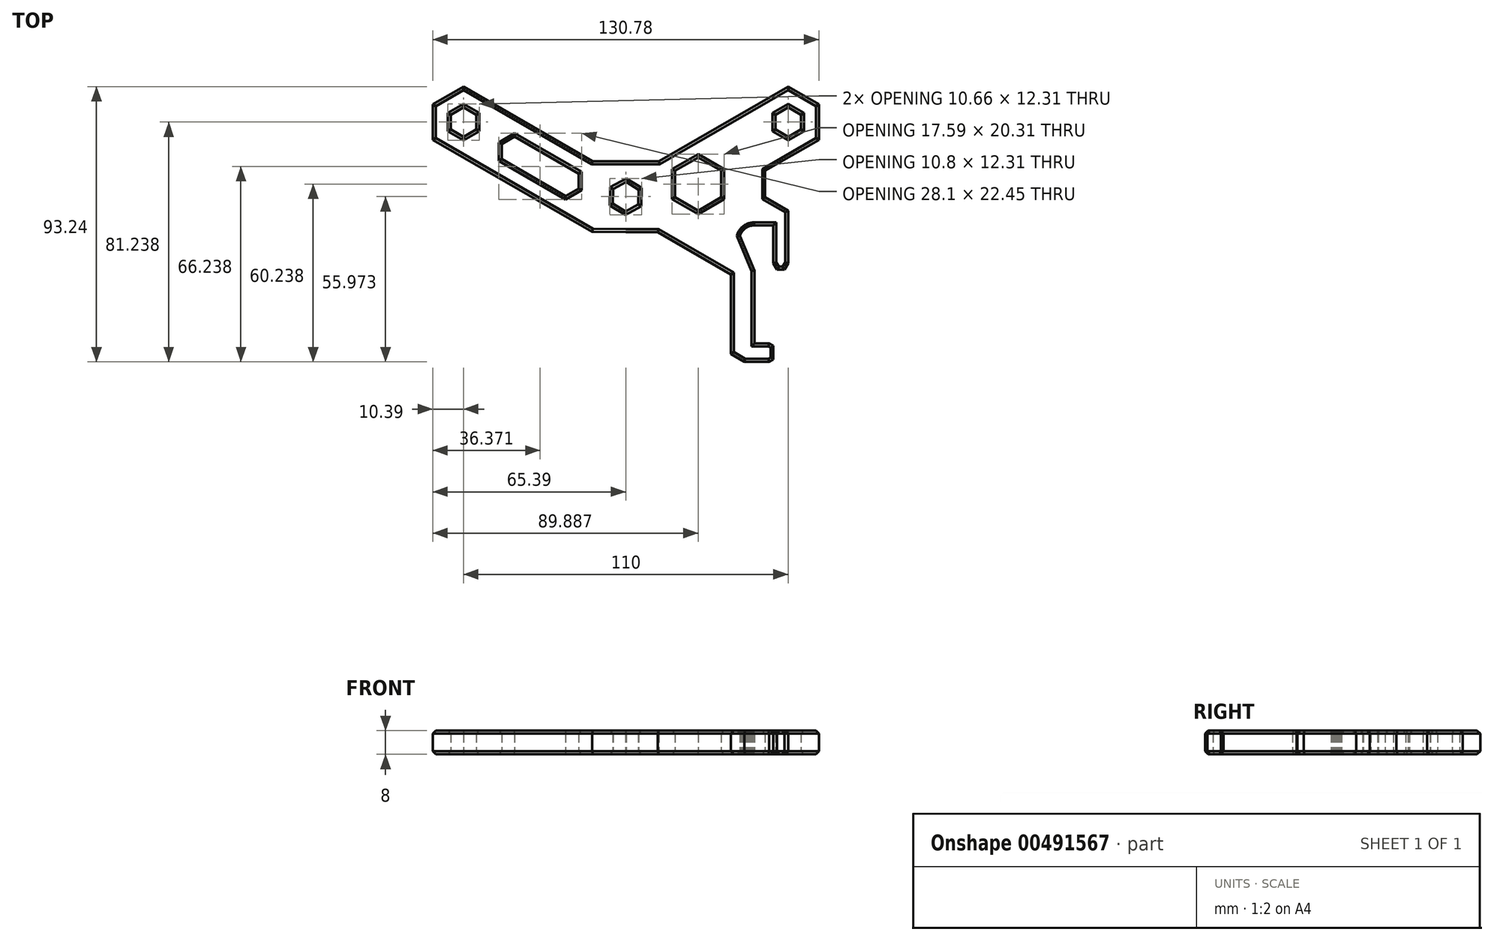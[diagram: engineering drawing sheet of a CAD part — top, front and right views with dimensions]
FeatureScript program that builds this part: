
annotation { "Feature Type Name" : "Feature", "Feature Type Description" : "" }
export const myFeature = defineFeature(function(context is Context, id is Id, definition is map)
    precondition{}
    {
        {
            var Q0;
            Q0=qCreatedBy(makeId("Top.planeOp"),FACE);
            var sketch = newSketch(context, id + "F0", { "sketchPlane" : qUnion([Q0])});
            skLineSegment(sketch, "E0", {"start": v(-65.4, 28.62) * mm, "end": v(-11.37, -2.57) * mm});
            skLineSegment(sketch, "E1", {"start": v(-11.37, -2.57) * mm, "end": v(0, -2.65) * mm});
            skLineSegment(sketch, "E2", {"start": v(0, -2.65) * mm, "end": v(10.81, -2.65) * mm});
            skLineSegment(sketch, "E3", {"start": v(10.81, -2.65) * mm, "end": v(35.6, -16.96) * mm});
            skLineSegment(sketch, "E4", {"start": v(35.6, -16.96) * mm, "end": v(35.6, -43.93) * mm});
            skLineSegment(sketch, "E5", {"start": v(35.6, -43.93) * mm, "end": v(40.17, -46.62) * mm});
            skLineSegment(sketch, "E6", {"start": v(40.17, -46.62) * mm, "end": v(48.6, -46.62) * mm});
            skLineSegment(sketch, "E7", {"start": v(48.6, -46.62) * mm, "end": v(50, -45.83) * mm});
            skLineSegment(sketch, "E8", {"start": v(50, -45.83) * mm, "end": v(50, -41.2) * mm});
            skLineSegment(sketch, "E9", {"start": v(50, -41.2) * mm, "end": v(48.6, -40.38) * mm});
            skLineSegment(sketch, "E10", {"start": v(48.6, -40.38) * mm, "end": v(43.6, -40.38) * mm});
            skLineSegment(sketch, "E11", {"start": v(43.6, -40.38) * mm, "end": v(43.6, -15.68) * mm});
            skLineSegment(sketch, "E12", {"start": v(43.6, -15.68) * mm, "end": v(38.65, -3.92) * mm});
            skLineSegment(sketch, "E13", {"start": v(38.65, -3.92) * mm, "end": v(38.7, -3.76) * mm});
            skLineSegment(sketch, "E14", {"start": v(38.7, -3.76) * mm, "end": v(38.77, -3.6) * mm});
            skLineSegment(sketch, "E15", {"start": v(38.77, -3.6) * mm, "end": v(38.83, -3.43) * mm});
            skLineSegment(sketch, "E16", {"start": v(38.83, -3.43) * mm, "end": v(38.9, -3.28) * mm});
            skLineSegment(sketch, "E17", {"start": v(38.9, -3.28) * mm, "end": v(38.98, -3.12) * mm});
            skLineSegment(sketch, "E18", {"start": v(38.98, -3.12) * mm, "end": v(39.06, -2.97) * mm});
            skLineSegment(sketch, "E19", {"start": v(39.06, -2.97) * mm, "end": v(39.15, -2.82) * mm});
            skLineSegment(sketch, "E20", {"start": v(39.15, -2.82) * mm, "end": v(39.24, -2.67) * mm});
            skLineSegment(sketch, "E21", {"start": v(39.24, -2.67) * mm, "end": v(39.34, -2.53) * mm});
            skLineSegment(sketch, "E22", {"start": v(39.34, -2.53) * mm, "end": v(39.44, -2.39) * mm});
            skLineSegment(sketch, "E23", {"start": v(39.44, -2.39) * mm, "end": v(39.55, -2.25) * mm});
            skLineSegment(sketch, "E24", {"start": v(39.55, -2.25) * mm, "end": v(39.66, -2.12) * mm});
            skLineSegment(sketch, "E25", {"start": v(39.66, -2.12) * mm, "end": v(39.77, -1.99) * mm});
            skLineSegment(sketch, "E26", {"start": v(39.77, -1.99) * mm, "end": v(39.9, -1.86) * mm});
            skLineSegment(sketch, "E27", {"start": v(39.9, -1.86) * mm, "end": v(40.02, -1.74) * mm});
            skLineSegment(sketch, "E28", {"start": v(40.02, -1.74) * mm, "end": v(40.15, -1.63) * mm});
            skLineSegment(sketch, "E29", {"start": v(40.15, -1.63) * mm, "end": v(40.28, -1.52) * mm});
            skLineSegment(sketch, "E30", {"start": v(40.28, -1.52) * mm, "end": v(40.42, -1.4) * mm});
            skLineSegment(sketch, "E31", {"start": v(40.42, -1.4) * mm, "end": v(40.56, -1.3) * mm});
            skLineSegment(sketch, "E32", {"start": v(40.56, -1.3) * mm, "end": v(40.7, -1.2) * mm});
            skLineSegment(sketch, "E33", {"start": v(40.7, -1.2) * mm, "end": v(40.85, -1.12) * mm});
            skLineSegment(sketch, "E34", {"start": v(40.85, -1.12) * mm, "end": v(41, -1.03) * mm});
            skLineSegment(sketch, "E35", {"start": v(41, -1.03) * mm, "end": v(41.15, -0.95) * mm});
            skLineSegment(sketch, "E36", {"start": v(41.15, -0.95) * mm, "end": v(41.3, -0.87) * mm});
            skLineSegment(sketch, "E37", {"start": v(41.3, -0.87) * mm, "end": v(41.46, -0.8) * mm});
            skLineSegment(sketch, "E38", {"start": v(41.46, -0.8) * mm, "end": v(41.62, -0.73) * mm});
            skLineSegment(sketch, "E39", {"start": v(41.62, -0.73) * mm, "end": v(41.78, -0.67) * mm});
            skLineSegment(sketch, "E40", {"start": v(41.78, -0.67) * mm, "end": v(41.95, -0.62) * mm});
            skLineSegment(sketch, "E41", {"start": v(41.95, -0.62) * mm, "end": v(42.12, -0.57) * mm});
            skLineSegment(sketch, "E42", {"start": v(42.12, -0.57) * mm, "end": v(42.28, -0.52) * mm});
            skLineSegment(sketch, "E43", {"start": v(42.28, -0.52) * mm, "end": v(42.45, -0.49) * mm});
            skLineSegment(sketch, "E44", {"start": v(42.45, -0.49) * mm, "end": v(42.62, -0.45) * mm});
            skLineSegment(sketch, "E45", {"start": v(42.62, -0.45) * mm, "end": v(42.8, -0.43) * mm});
            skLineSegment(sketch, "E46", {"start": v(42.8, -0.43) * mm, "end": v(42.97, -0.4) * mm});
            skLineSegment(sketch, "E47", {"start": v(42.97, -0.4) * mm, "end": v(43.14, -0.4) * mm});
            skLineSegment(sketch, "E48", {"start": v(43.14, -0.4) * mm, "end": v(43.31, -0.39) * mm});
            skLineSegment(sketch, "E49", {"start": v(43.31, -0.39) * mm, "end": v(43.49, -0.38) * mm});
            skLineSegment(sketch, "E50", {"start": v(43.49, -0.38) * mm, "end": v(50, -0.38) * mm});
            skLineSegment(sketch, "E51", {"start": v(50, -0.38) * mm, "end": v(50, -13.16) * mm});
            skLineSegment(sketch, "E52", {"start": v(50, -13.16) * mm, "end": v(51.25, -15.33) * mm});
            skLineSegment(sketch, "E53", {"start": v(51.25, -15.33) * mm, "end": v(53.75, -15.33) * mm});
            skLineSegment(sketch, "E54", {"start": v(53.75, -15.33) * mm, "end": v(55, -13.16) * mm});
            skLineSegment(sketch, "E55", {"start": v(55, -13.16) * mm, "end": v(55, 4.62) * mm});
            skLineSegment(sketch, "E56", {"start": v(55, 4.62) * mm, "end": v(47.2, 9.12) * mm});
            skLineSegment(sketch, "E57", {"start": v(47.2, 9.12) * mm, "end": v(47.2, 18.12) * mm});
            skLineSegment(sketch, "E58", {"start": v(47.2, 18.12) * mm, "end": v(55, 22.62) * mm});
            skLineSegment(sketch, "E59", {"start": v(55, 22.62) * mm, "end": v(65.4, 28.62) * mm});
            skLineSegment(sketch, "E60", {"start": v(65.4, 28.62) * mm, "end": v(65.4, 40.62) * mm});
            skLineSegment(sketch, "E61", {"start": v(65.4, 40.62) * mm, "end": v(55, 46.62) * mm});
            skLineSegment(sketch, "E62", {"start": v(55, 46.62) * mm, "end": v(11.24, 21.35) * mm});
            skLineSegment(sketch, "E63", {"start": v(11.24, 21.35) * mm, "end": v(-11.24, 21.35) * mm});
            skLineSegment(sketch, "E64", {"start": v(-11.24, 21.35) * mm, "end": v(-55, 46.62) * mm});
            skLineSegment(sketch, "E65", {"start": v(-55, 46.62) * mm, "end": v(-65.4, 40.62) * mm});
            skLineSegment(sketch, "E66", {"start": v(-65.4, 40.62) * mm, "end": v(-65.4, 28.62) * mm});
            skLineSegment(sketch, "E67", {"start": v(-59.33, 32.12) * mm, "end": v(-59.33, 37.12) * mm});
            skLineSegment(sketch, "E68", {"start": v(-59.33, 37.12) * mm, "end": v(-55, 39.62) * mm});
            skLineSegment(sketch, "E69", {"start": v(-55, 39.62) * mm, "end": v(-50.67, 37.12) * mm});
            skLineSegment(sketch, "E70", {"start": v(-50.67, 37.12) * mm, "end": v(-50.67, 32.12) * mm});
            skLineSegment(sketch, "E71", {"start": v(-50.67, 32.12) * mm, "end": v(-55, 29.62) * mm});
            skLineSegment(sketch, "E72", {"start": v(-55, 29.62) * mm, "end": v(-59.33, 32.12) * mm});
            skLineSegment(sketch, "E73", {"start": v(-42.07, 22.08) * mm, "end": v(-42.07, 27.15) * mm});
            skLineSegment(sketch, "E74", {"start": v(-42.07, 27.15) * mm, "end": v(-37.68, 29.69) * mm});
            skLineSegment(sketch, "E75", {"start": v(-37.68, 29.69) * mm, "end": v(-15.97, 17.15) * mm});
            skLineSegment(sketch, "E76", {"start": v(-15.97, 17.15) * mm, "end": v(-15.97, 12.08) * mm});
            skLineSegment(sketch, "E77", {"start": v(-15.97, 12.08) * mm, "end": v(-20.36, 9.55) * mm});
            skLineSegment(sketch, "E78", {"start": v(-20.36, 9.55) * mm, "end": v(-42.07, 22.08) * mm});
            skLineSegment(sketch, "E79", {"start": v(-4.39, 6.96) * mm, "end": v(-4.27, 11.95) * mm});
            skLineSegment(sketch, "E80", {"start": v(-4.27, 11.95) * mm, "end": v(0.12, 14.35) * mm});
            skLineSegment(sketch, "E81", {"start": v(0.12, 14.35) * mm, "end": v(4.39, 11.75) * mm});
            skLineSegment(sketch, "E82", {"start": v(4.39, 11.75) * mm, "end": v(4.27, 6.75) * mm});
            skLineSegment(sketch, "E83", {"start": v(4.27, 6.75) * mm, "end": v(-0.12, 4.35) * mm});
            skLineSegment(sketch, "E84", {"start": v(-0.12, 4.35) * mm, "end": v(-4.39, 6.96) * mm});
            skLineSegment(sketch, "E85", {"start": v(16.7, 9.12) * mm, "end": v(16.7, 18.12) * mm});
            skLineSegment(sketch, "E86", {"start": v(16.7, 18.12) * mm, "end": v(24.5, 22.62) * mm});
            skLineSegment(sketch, "E87", {"start": v(24.5, 22.62) * mm, "end": v(32.3, 18.12) * mm});
            skLineSegment(sketch, "E88", {"start": v(32.3, 18.12) * mm, "end": v(32.3, 9.12) * mm});
            skLineSegment(sketch, "E89", {"start": v(32.3, 9.12) * mm, "end": v(24.5, 4.62) * mm});
            skLineSegment(sketch, "E90", {"start": v(24.5, 4.62) * mm, "end": v(16.7, 9.12) * mm});
            skLineSegment(sketch, "E91", {"start": v(50.67, 32.12) * mm, "end": v(50.67, 37.12) * mm});
            skLineSegment(sketch, "E92", {"start": v(50.67, 37.12) * mm, "end": v(55, 39.62) * mm});
            skLineSegment(sketch, "E93", {"start": v(55, 39.62) * mm, "end": v(59.33, 37.12) * mm});
            skLineSegment(sketch, "E94", {"start": v(59.33, 37.12) * mm, "end": v(59.33, 32.12) * mm});
            skLineSegment(sketch, "E95", {"start": v(59.33, 32.12) * mm, "end": v(55, 29.62) * mm});
            skLineSegment(sketch, "E96", {"start": v(55, 29.62) * mm, "end": v(50.67, 32.12) * mm});
            skSolve(sketch);
        }
        {
            var Q0;
            Q0 = qSketchRegion(id + "F0", true);
            extrude(context, id + "F1", {"entities" : qUnion([Q0]), "depth" : 8 * mm, "offsetDistance" : 25 * mm});
        }
        {
            var Q0;
            Q0=makeQuery(id+"F1.opExtrude","CAP_FACE",FACE,{"disambiguationData":[OSD([sQuery(id+"F0.wireOp",EDGE,"E0"),sQuery(id+"F0.wireOp",EDGE,"E1"),sQuery(id+"F0.wireOp",EDGE,"E2"),sQuery(id+"F0.wireOp",EDGE,"E3"),sQuery(id+"F0.wireOp",EDGE,"E4"),sQuery(id+"F0.wireOp",EDGE,"E5"),sQuery(id+"F0.wireOp",EDGE,"E6"),sQuery(id+"F0.wireOp",EDGE,"E7"),sQuery(id+"F0.wireOp",EDGE,"E8"),sQuery(id+"F0.wireOp",EDGE,"E9"),sQuery(id+"F0.wireOp",EDGE,"E10"),sQuery(id+"F0.wireOp",EDGE,"E11"),sQuery(id+"F0.wireOp",EDGE,"E12"),sQuery(id+"F0.wireOp",EDGE,"E13"),sQuery(id+"F0.wireOp",EDGE,"E14"),sQuery(id+"F0.wireOp",EDGE,"E15"),sQuery(id+"F0.wireOp",EDGE,"E16"),sQuery(id+"F0.wireOp",EDGE,"E17"),sQuery(id+"F0.wireOp",EDGE,"E18"),sQuery(id+"F0.wireOp",EDGE,"E19"),sQuery(id+"F0.wireOp",EDGE,"E20"),sQuery(id+"F0.wireOp",EDGE,"E21"),sQuery(id+"F0.wireOp",EDGE,"E22"),sQuery(id+"F0.wireOp",EDGE,"E23"),sQuery(id+"F0.wireOp",EDGE,"E24"),sQuery(id+"F0.wireOp",EDGE,"E25"),sQuery(id+"F0.wireOp",EDGE,"E26"),sQuery(id+"F0.wireOp",EDGE,"E27"),sQuery(id+"F0.wireOp",EDGE,"E28"),sQuery(id+"F0.wireOp",EDGE,"E29"),sQuery(id+"F0.wireOp",EDGE,"E30"),sQuery(id+"F0.wireOp",EDGE,"E31"),sQuery(id+"F0.wireOp",EDGE,"E32"),sQuery(id+"F0.wireOp",EDGE,"E33"),sQuery(id+"F0.wireOp",EDGE,"E34"),sQuery(id+"F0.wireOp",EDGE,"E35"),sQuery(id+"F0.wireOp",EDGE,"E36"),sQuery(id+"F0.wireOp",EDGE,"E37"),sQuery(id+"F0.wireOp",EDGE,"E38"),sQuery(id+"F0.wireOp",EDGE,"E39"),sQuery(id+"F0.wireOp",EDGE,"E40"),sQuery(id+"F0.wireOp",EDGE,"E41"),sQuery(id+"F0.wireOp",EDGE,"E42"),sQuery(id+"F0.wireOp",EDGE,"E43"),sQuery(id+"F0.wireOp",EDGE,"E44"),sQuery(id+"F0.wireOp",EDGE,"E45"),sQuery(id+"F0.wireOp",EDGE,"E46"),sQuery(id+"F0.wireOp",EDGE,"E47"),sQuery(id+"F0.wireOp",EDGE,"E48"),sQuery(id+"F0.wireOp",EDGE,"E49"),sQuery(id+"F0.wireOp",EDGE,"E50"),sQuery(id+"F0.wireOp",EDGE,"E51"),sQuery(id+"F0.wireOp",EDGE,"E52"),sQuery(id+"F0.wireOp",EDGE,"E53"),sQuery(id+"F0.wireOp",EDGE,"E54"),sQuery(id+"F0.wireOp",EDGE,"E55"),sQuery(id+"F0.wireOp",EDGE,"E56"),sQuery(id+"F0.wireOp",EDGE,"E57"),sQuery(id+"F0.wireOp",EDGE,"E58"),sQuery(id+"F0.wireOp",EDGE,"E59"),sQuery(id+"F0.wireOp",EDGE,"E60"),sQuery(id+"F0.wireOp",EDGE,"E61"),sQuery(id+"F0.wireOp",EDGE,"E62"),sQuery(id+"F0.wireOp",EDGE,"E63"),sQuery(id+"F0.wireOp",EDGE,"E64"),sQuery(id+"F0.wireOp",EDGE,"E65"),sQuery(id+"F0.wireOp",EDGE,"E66"),sQuery(id+"F0.wireOp",EDGE,"E67"),sQuery(id+"F0.wireOp",EDGE,"E68"),sQuery(id+"F0.wireOp",EDGE,"E69"),sQuery(id+"F0.wireOp",EDGE,"E70"),sQuery(id+"F0.wireOp",EDGE,"E71"),sQuery(id+"F0.wireOp",EDGE,"E72"),sQuery(id+"F0.wireOp",EDGE,"E73"),sQuery(id+"F0.wireOp",EDGE,"E74"),sQuery(id+"F0.wireOp",EDGE,"E75"),sQuery(id+"F0.wireOp",EDGE,"E76"),sQuery(id+"F0.wireOp",EDGE,"E77"),sQuery(id+"F0.wireOp",EDGE,"E78"),sQuery(id+"F0.wireOp",EDGE,"E79"),sQuery(id+"F0.wireOp",EDGE,"E80"),sQuery(id+"F0.wireOp",EDGE,"E81"),sQuery(id+"F0.wireOp",EDGE,"E82"),sQuery(id+"F0.wireOp",EDGE,"E83"),sQuery(id+"F0.wireOp",EDGE,"E84"),sQuery(id+"F0.wireOp",EDGE,"E85"),sQuery(id+"F0.wireOp",EDGE,"E86"),sQuery(id+"F0.wireOp",EDGE,"E87"),sQuery(id+"F0.wireOp",EDGE,"E88"),sQuery(id+"F0.wireOp",EDGE,"E89"),sQuery(id+"F0.wireOp",EDGE,"E90"),sQuery(id+"F0.wireOp",EDGE,"E91"),sQuery(id+"F0.wireOp",EDGE,"E92"),sQuery(id+"F0.wireOp",EDGE,"E93"),sQuery(id+"F0.wireOp",EDGE,"E94"),sQuery(id+"F0.wireOp",EDGE,"E95"),sQuery(id+"F0.wireOp",EDGE,"E96")])],"isStart":false});
            var Q1;
            Q1=makeQuery(id+"F1.opExtrude","CAP_FACE",FACE,{"disambiguationData":[OSD([sQuery(id+"F0.wireOp",EDGE,"E0"),sQuery(id+"F0.wireOp",EDGE,"E1"),sQuery(id+"F0.wireOp",EDGE,"E2"),sQuery(id+"F0.wireOp",EDGE,"E3"),sQuery(id+"F0.wireOp",EDGE,"E4"),sQuery(id+"F0.wireOp",EDGE,"E5"),sQuery(id+"F0.wireOp",EDGE,"E6"),sQuery(id+"F0.wireOp",EDGE,"E7"),sQuery(id+"F0.wireOp",EDGE,"E8"),sQuery(id+"F0.wireOp",EDGE,"E9"),sQuery(id+"F0.wireOp",EDGE,"E10"),sQuery(id+"F0.wireOp",EDGE,"E11"),sQuery(id+"F0.wireOp",EDGE,"E12"),sQuery(id+"F0.wireOp",EDGE,"E13"),sQuery(id+"F0.wireOp",EDGE,"E14"),sQuery(id+"F0.wireOp",EDGE,"E15"),sQuery(id+"F0.wireOp",EDGE,"E16"),sQuery(id+"F0.wireOp",EDGE,"E17"),sQuery(id+"F0.wireOp",EDGE,"E18"),sQuery(id+"F0.wireOp",EDGE,"E19"),sQuery(id+"F0.wireOp",EDGE,"E20"),sQuery(id+"F0.wireOp",EDGE,"E21"),sQuery(id+"F0.wireOp",EDGE,"E22"),sQuery(id+"F0.wireOp",EDGE,"E23"),sQuery(id+"F0.wireOp",EDGE,"E24"),sQuery(id+"F0.wireOp",EDGE,"E25"),sQuery(id+"F0.wireOp",EDGE,"E26"),sQuery(id+"F0.wireOp",EDGE,"E27"),sQuery(id+"F0.wireOp",EDGE,"E28"),sQuery(id+"F0.wireOp",EDGE,"E29"),sQuery(id+"F0.wireOp",EDGE,"E30"),sQuery(id+"F0.wireOp",EDGE,"E31"),sQuery(id+"F0.wireOp",EDGE,"E32"),sQuery(id+"F0.wireOp",EDGE,"E33"),sQuery(id+"F0.wireOp",EDGE,"E34"),sQuery(id+"F0.wireOp",EDGE,"E35"),sQuery(id+"F0.wireOp",EDGE,"E36"),sQuery(id+"F0.wireOp",EDGE,"E37"),sQuery(id+"F0.wireOp",EDGE,"E38"),sQuery(id+"F0.wireOp",EDGE,"E39"),sQuery(id+"F0.wireOp",EDGE,"E40"),sQuery(id+"F0.wireOp",EDGE,"E41"),sQuery(id+"F0.wireOp",EDGE,"E42"),sQuery(id+"F0.wireOp",EDGE,"E43"),sQuery(id+"F0.wireOp",EDGE,"E44"),sQuery(id+"F0.wireOp",EDGE,"E45"),sQuery(id+"F0.wireOp",EDGE,"E46"),sQuery(id+"F0.wireOp",EDGE,"E47"),sQuery(id+"F0.wireOp",EDGE,"E48"),sQuery(id+"F0.wireOp",EDGE,"E49"),sQuery(id+"F0.wireOp",EDGE,"E50"),sQuery(id+"F0.wireOp",EDGE,"E51"),sQuery(id+"F0.wireOp",EDGE,"E52"),sQuery(id+"F0.wireOp",EDGE,"E53"),sQuery(id+"F0.wireOp",EDGE,"E54"),sQuery(id+"F0.wireOp",EDGE,"E55"),sQuery(id+"F0.wireOp",EDGE,"E56"),sQuery(id+"F0.wireOp",EDGE,"E57"),sQuery(id+"F0.wireOp",EDGE,"E58"),sQuery(id+"F0.wireOp",EDGE,"E59"),sQuery(id+"F0.wireOp",EDGE,"E60"),sQuery(id+"F0.wireOp",EDGE,"E61"),sQuery(id+"F0.wireOp",EDGE,"E62"),sQuery(id+"F0.wireOp",EDGE,"E63"),sQuery(id+"F0.wireOp",EDGE,"E64"),sQuery(id+"F0.wireOp",EDGE,"E65"),sQuery(id+"F0.wireOp",EDGE,"E66"),sQuery(id+"F0.wireOp",EDGE,"E67"),sQuery(id+"F0.wireOp",EDGE,"E68"),sQuery(id+"F0.wireOp",EDGE,"E69"),sQuery(id+"F0.wireOp",EDGE,"E70"),sQuery(id+"F0.wireOp",EDGE,"E71"),sQuery(id+"F0.wireOp",EDGE,"E72"),sQuery(id+"F0.wireOp",EDGE,"E73"),sQuery(id+"F0.wireOp",EDGE,"E74"),sQuery(id+"F0.wireOp",EDGE,"E75"),sQuery(id+"F0.wireOp",EDGE,"E76"),sQuery(id+"F0.wireOp",EDGE,"E77"),sQuery(id+"F0.wireOp",EDGE,"E78"),sQuery(id+"F0.wireOp",EDGE,"E79"),sQuery(id+"F0.wireOp",EDGE,"E80"),sQuery(id+"F0.wireOp",EDGE,"E81"),sQuery(id+"F0.wireOp",EDGE,"E82"),sQuery(id+"F0.wireOp",EDGE,"E83"),sQuery(id+"F0.wireOp",EDGE,"E84"),sQuery(id+"F0.wireOp",EDGE,"E85"),sQuery(id+"F0.wireOp",EDGE,"E86"),sQuery(id+"F0.wireOp",EDGE,"E87"),sQuery(id+"F0.wireOp",EDGE,"E88"),sQuery(id+"F0.wireOp",EDGE,"E89"),sQuery(id+"F0.wireOp",EDGE,"E90"),sQuery(id+"F0.wireOp",EDGE,"E91"),sQuery(id+"F0.wireOp",EDGE,"E92"),sQuery(id+"F0.wireOp",EDGE,"E93"),sQuery(id+"F0.wireOp",EDGE,"E94"),sQuery(id+"F0.wireOp",EDGE,"E95"),sQuery(id+"F0.wireOp",EDGE,"E96")])],"isStart":true});
            chamfer(context, id + "F2", {"entities" : qUnion([Q0, Q1]), "width" : 1 * mm, "tangentPropagation" : true});
        }
    });
